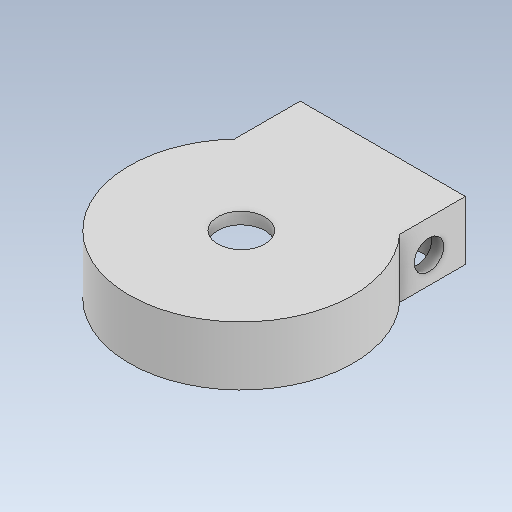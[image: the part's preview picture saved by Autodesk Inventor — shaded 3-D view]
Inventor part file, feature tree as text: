
AUTODESK INVENTOR PART (.ipt)
format: ipt  version: 2021.2 (Build 252289000, 289)  size: 150,016 bytes
history: native  units: in
note: dims shown in document units (in); Inventor stores cm internally (conversion verified against a paired STEP export)
features: reference x6, extrude x5, sketch x3, other x3, mirror x1
ambient origin geometry x8: Origin, YZ Plane, XZ Plane, XY Plane, X Axis, Y Axis, Z Axis, Center Point
bodies: Solid1 (feature_tree)
feature tree (18):
  extrude  "Extrusion1"  Depth=0.25in TaperAngle=0.0deg
  sketch  "Sketch3"  dims[d0=4.25in d1=0.25in d2=0.0in]
  extrude  "Extrusion3"  Depth=1.5in
  extrude  "Extrusion4"  Depth=0.25in
  extrude  "Extrusion6"  Depth=0.25in
  mirror  "Mirror1"
  extrude  "Extrusion7"  Depth=0.25in
  sketch  "Sketch4"  dims[d6=2.75in d7=1.5in]
  reference  "Reference1"
  reference  "Reference2"
  reference  "Reference3"
  reference  "Reference4"
  reference  "Reference5"
  reference  "Reference6"
  sketch  "Sketch5"  dims[d8=0.25in d9=0.25in d10=0.25in d11=0.25in d12=1.0in d13=0.0in d14=0.25in d15=0.0in d20=0.625in d21=0.375in d22=0.0in d23=0.0in d24=1.0in d25=0.0in d26=0.0in]
  other  "forkMountForDecTripV03.iam"
  other  "Worm Gears:2"
  other  "Worm:1"
